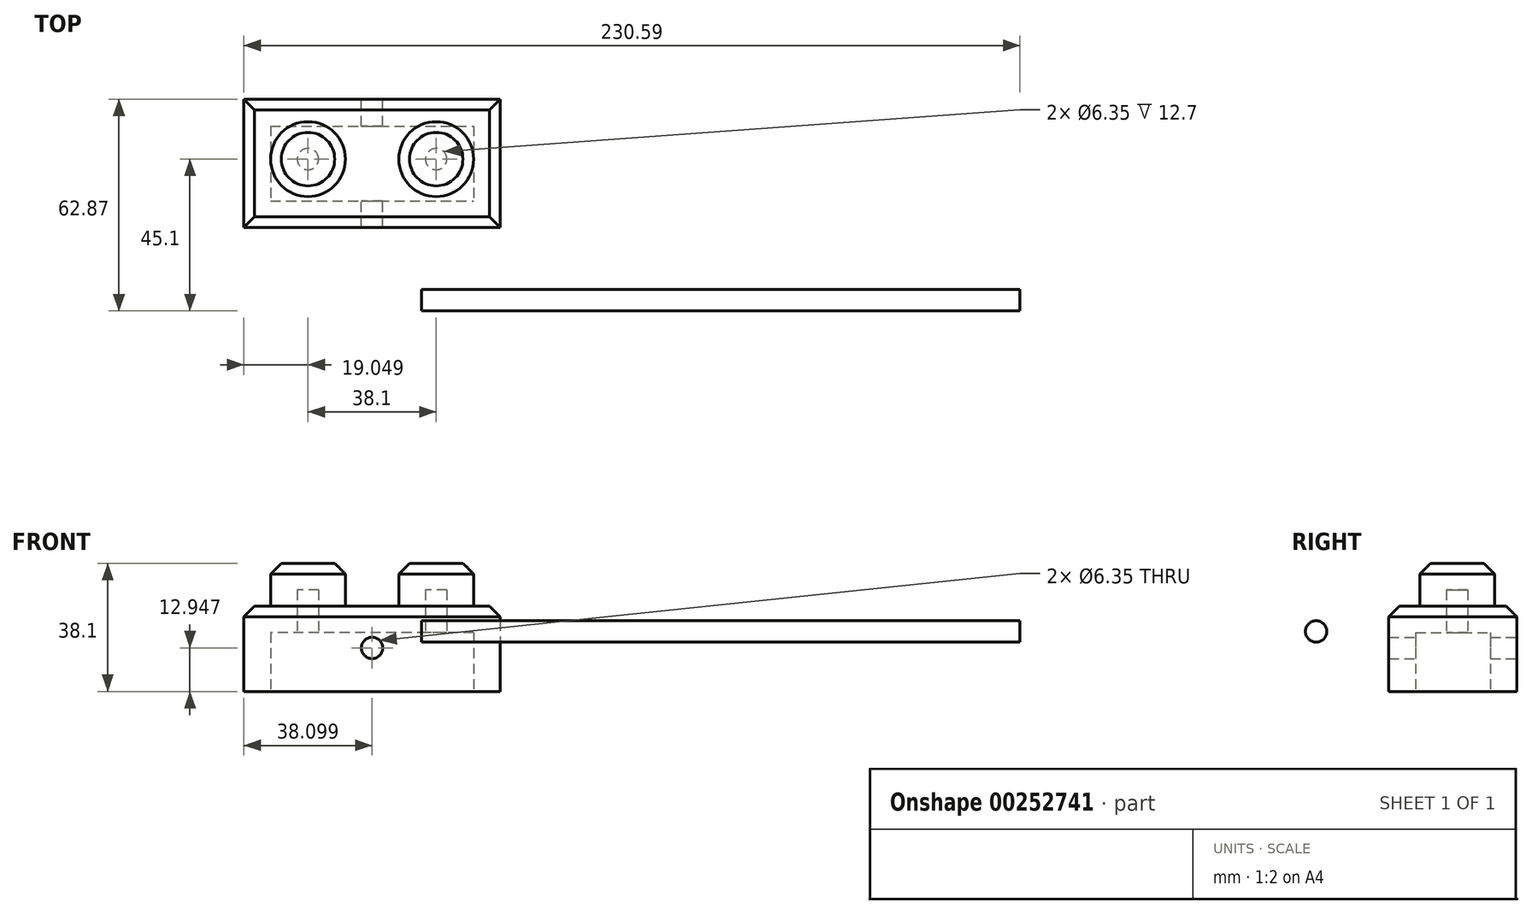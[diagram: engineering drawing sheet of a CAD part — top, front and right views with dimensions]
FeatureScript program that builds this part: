
annotation { "Feature Type Name" : "Feature", "Feature Type Description" : "" }
export const myFeature = defineFeature(function(context is Context, id is Id, definition is map)
    precondition{}
    {
        {
            var Q0;
            Q0=qCreatedBy(makeId("Top.planeOp"),FACE);
            var sketch = newSketch(context, id + "F0", { "sketchPlane" : qUnion([Q0])});
            skLineSegment(sketch, "E0.bottom", {"start": v(-52.8, 17.77) * mm, "end": v(23.4, 17.77) * mm});
            skLineSegment(sketch, "E0.top", {"start": v(-52.8, -20.33) * mm, "end": v(23.4, -20.33) * mm});
            skLineSegment(sketch, "E0.left", {"start": v(-52.8, 17.77) * mm, "end": v(-52.8, -20.33) * mm});
            skLineSegment(sketch, "E0.right", {"start": v(23.4, 17.77) * mm, "end": v(23.4, -20.33) * mm});
            skSolve(sketch);
        }
        {
            var Q0;
            Q0 = qSketchRegion(id + "F0", true);
            extrude(context, id + "F1", {"entities" : qUnion([Q0]), "depth" : 25.4 * mm});
        }
        {
            var Q0;
            Q0=makeQuery(id+"F1.opExtrude","CAP_FACE",FACE,{"disambiguationData":[OSD([sQuery(id+"F0.wireOp",EDGE,"E0.bottom"),sQuery(id+"F0.wireOp",EDGE,"E0.top"),sQuery(id+"F0.wireOp",EDGE,"E0.left"),sQuery(id+"F0.wireOp",EDGE,"E0.right")])],"isStart":false});
            var sketch = newSketch(context, id + "F2", { "sketchPlane" : qUnion([Q0])});
            skCircle(sketch, "E1", {"center": v(-33.74, 0) * mm, "radius": 11.11 * mm});
            skCircle(sketch, "E2", {"center": v(4.36, 0) * mm, "radius": 11.11 * mm});
            skSolve(sketch);
        }
        {
            var Q0;
            Q0=makeQuery(id+"F2.imprint","IMPRINT",FACE,{"disambiguationData":[TD([[makeQuery(id+"F2.imprint","IMPRINT",EDGE,{"derivedFrom":sQuery(id+"F2.wireOp",EDGE,"E1")}),1.0]])]});
            var Q1;
            Q1=makeQuery(id+"F2.imprint","IMPRINT",FACE,{"disambiguationData":[TD([[makeQuery(id+"F2.imprint","IMPRINT",EDGE,{"derivedFrom":sQuery(id+"F2.wireOp",EDGE,"E2")}),1.0]])]});
            extrude(context, id + "F3", {"entities" : qUnion([Q0, Q1]), "operationType" : NewBodyOperationType.ADD, "depth" : 12.7 * mm});
        }
        {
            var Q0;
            Q0=makeQuery(id+"F1.opExtrude","CAP_EDGE",EDGE,{"disambiguationData":[OSD([sQuery(id+"F0.wireOp",EDGE,"E0.top")])],"isStart":false});
            var Q1;
            Q1=makeQuery(id+"F1.opExtrude","CAP_EDGE",EDGE,{"disambiguationData":[OSD([sQuery(id+"F0.wireOp",EDGE,"E0.left")])],"isStart":false});
            var Q2;
            Q2=makeQuery(id+"F1.opExtrude","CAP_EDGE",EDGE,{"disambiguationData":[OSD([sQuery(id+"F0.wireOp",EDGE,"E0.bottom")])],"isStart":false});
            var Q3;
            Q3=makeQuery(id+"F1.opExtrude","CAP_EDGE",EDGE,{"disambiguationData":[OSD([sQuery(id+"F0.wireOp",EDGE,"E0.right")])],"isStart":false});
            chamfer(context, id + "F4", {"entities" : qUnion([Q0, Q1, Q2, Q3]), "chamferType" : ChamferType.OFFSET_ANGLE, "width" : 3.17 * mm, "oppositeDirection" : false, "angle" : 45 * degree, "tangentPropagation" : true});
        }
        {
            var Q0;
            Q0=makeQuery(id+"F3.opExtrude","CAP_FACE",FACE,{"disambiguationData":[OSD([sQuery(id+"F2.wireOp",EDGE,"E1")])],"isStart":false});
            var Q1;
            Q1=makeQuery(id+"F3.opExtrude","CAP_EDGE",EDGE,{"disambiguationData":[OSD([sQuery(id+"F2.wireOp",EDGE,"E2")])],"isStart":false});
            chamfer(context, id + "F5", {"entities" : qUnion([Q0, Q1]), "width" : 3.17 * mm, "tangentPropagation" : true});
        }
        {
            var Q0;
            Q0=makeQuery(id+"F1.opExtrude","CAP_FACE",FACE,{"disambiguationData":[OSD([sQuery(id+"F0.wireOp",EDGE,"E0.bottom"),sQuery(id+"F0.wireOp",EDGE,"E0.top"),sQuery(id+"F0.wireOp",EDGE,"E0.left"),sQuery(id+"F0.wireOp",EDGE,"E0.right")])],"isStart":true});
            shell(context, id + "F6", {"entities" : qUnion([Q0]), "thickness" : 7.94 * mm});
        }
        {
            var Q0;
            Q0=qCreatedBy(makeId("Front.planeOp"),FACE);
            var sketch = newSketch(context, id + "F7", { "sketchPlane" : qUnion([Q0])});
            skCircle(sketch, "E3", {"center": v(-14.7, 12.95) * mm, "radius": 3.18 * mm});
            skSolve(sketch);
        }
        {
            var Q0;
            Q0 = qSketchRegion(id + "F7", true);
            extrude(context, id + "F8", {"entities" : qUnion([Q0]), "operationType" : NewBodyOperationType.REMOVE, "endBound" : BoundingType.THROUGH_ALL, "depth" : 25.4 * mm, "hasSecondDirection" : true, "secondDirectionBound" : SecondDirectionBoundingType.THROUGH_ALL, "secondDirectionOppositeDirection" : true, "secondDirectionDepth" : 25.4 * mm});
        }
        {
            var Q0;
            Q0=qCreatedBy(makeId("Right.planeOp"),FACE);
            var sketch = newSketch(context, id + "F9", { "sketchPlane" : qUnion([Q0])});
            skCircle(sketch, "E4", {"center": v(-41.92, 17.83) * mm, "radius": 3.18 * mm});
            skSolve(sketch);
        }
        {
            var Q0;
            Q0 = qSketchRegion(id + "F9", true);
            extrude(context, id + "F10", {"entities" : qUnion([Q0]), "depth" : 177.8 * mm});
        }
    });
